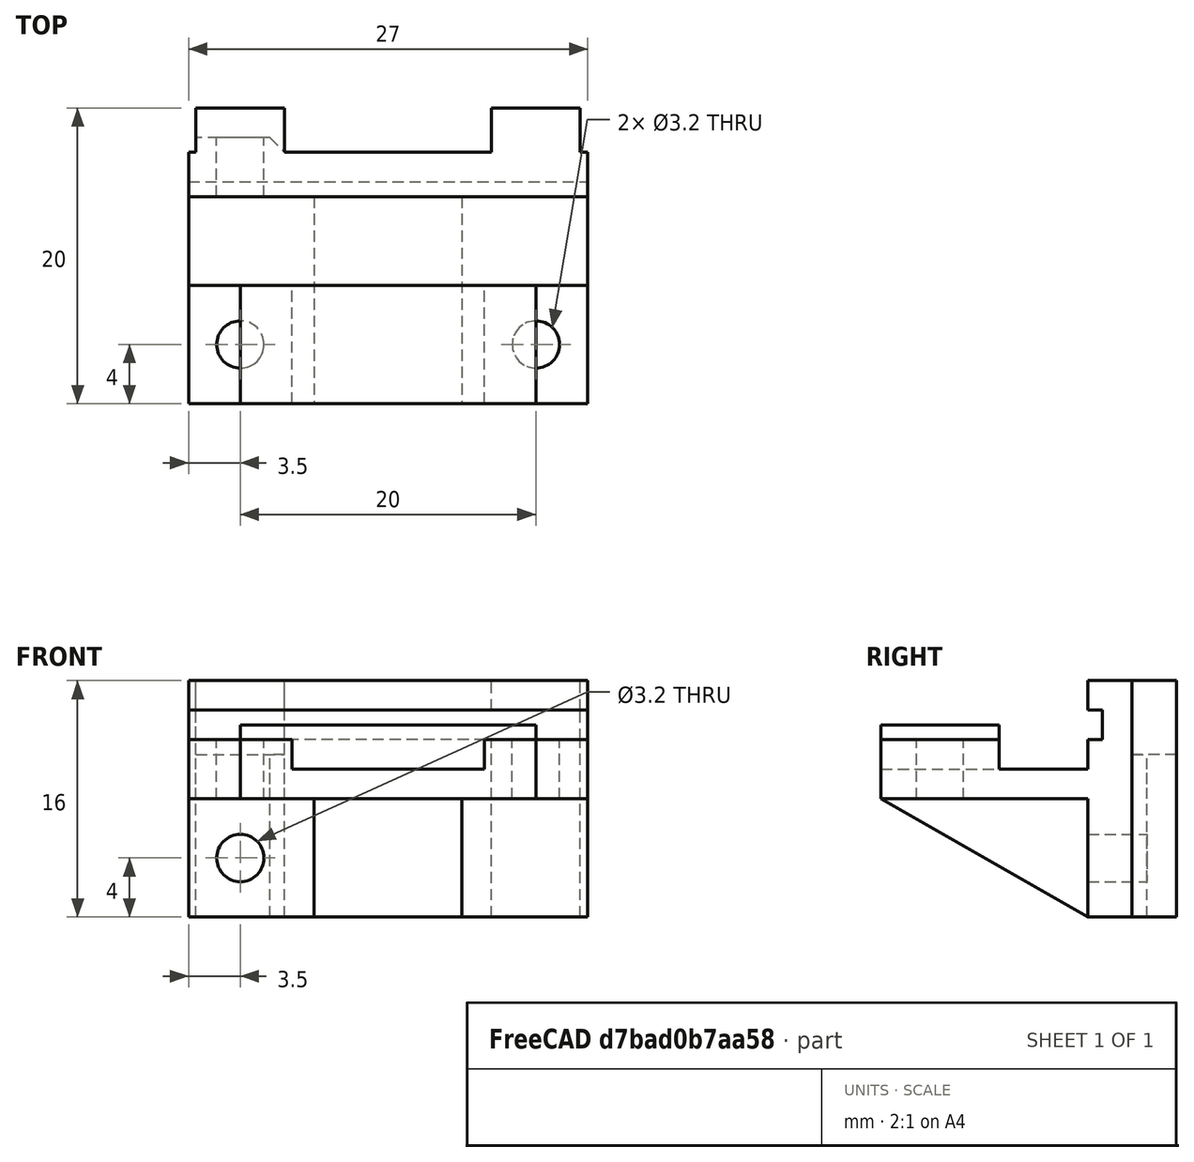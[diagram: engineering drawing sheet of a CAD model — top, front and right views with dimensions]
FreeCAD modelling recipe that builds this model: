
FCSTD DOCUMENT  (FreeCAD 0.18R14555 (Git shallow))
Label: dual-z-motor-mounter
License: All rights reserved
LicenseURL: http://en.wikipedia.org/wiki/All_rights_reserved
objects: Part::Box×15, Part::MultiFuse×5, Part::Cut×5, Part::Cylinder×3, Part::Feature×3, Part::Chamfer×1, Part::MultiCommon×1
note: 33 computed .brp shape members not serialized (recipe doc carries the construction recipe); baked Part::Feature solids carry a one-line shape summary decoded from their .brp

FEATURE [Part::Box] Box  label="Cube"
  AttacherType = Attacher::AttachEngine3D
  Height = 5
  Length = 27
  Width = 15
FEATURE [Part::Box] Box001  label="Cube001"
  AttacherType = Attacher::AttachEngine3D
  Height = 5
  Length = 27
  Placement = pos=(0,15,0) rot=(0,0,1;0rad)
  Width = 2
FEATURE [Part::Box] Box002  label="Cube002"
  AttacherType = Attacher::AttachEngine3D
  Height = 2
  Length = 27
  Placement = pos=(0,15,5) rot=(0,0,1;0rad)
  Width = 2
FEATURE [Part::Box] Box003  label="Cube003"
  AttacherType = Attacher::AttachEngine3D
  Height = 2
  Length = 27
  Placement = pos=(0,14,7) rot=(0,0,1;0rad)
  Width = 3
FEATURE [Part::Box] Box004  label="Cube004"
  AttacherType = Attacher::AttachEngine3D
  Height = 3
  Length = 13
  Placement = pos=(7,0,2) rot=(0,0,1;0rad)
  Width = 8
FEATURE [Part::Box] Box005  label="Cube005"
  AttacherType = Attacher::AttachEngine3D
  Height = 3
  Length = 27
  Placement = pos=(0,8,2) rot=(0,0,1;0rad)
  Width = 6
FEATURE [Part::MultiFuse] Fusion
  Placement = pos=(0,0,1) rot=(0,0,1;0rad)
  Shapes = -> [Box005,Box004]
FEATURE [Part::Box] Box006  label="Cube006"
  AttacherType = Attacher::AttachEngine3D
  Height = 5
  Length = 20
  Placement = pos=(3.5,0,0) rot=(0,0,1;0rad)
  Width = 8
FEATURE [Part::Cylinder] Cylinder
  Angle = 360
  AttacherType = Attacher::AttachEngine3D
  Height = 5
  Placement = pos=(3.5,4,0) rot=(0,0,1;0rad)
  Radius = 1.6
FEATURE [Part::Cylinder] Cylinder001
  Angle = 360
  AttacherType = Attacher::AttachEngine3D
  Height = 5
  Placement = pos=(23.5,4,0) rot=(0,0,1;0rad)
  Radius = 1.6
FEATURE [Part::MultiFuse] Fusion002
  Shapes = -> [Cylinder001,Cylinder]
FEATURE [Part::MultiFuse] Fusion003
  Shapes = -> [Box002,Box,Box001,Box003]
FEATURE [Part::Cut] Cut
  Base = -> Fusion003
  Tool = -> Fusion
FEATURE [Part::Cut] Cut001
  Base = -> Cut
  Tool = -> Fusion002
FEATURE [Part::Box] Box007  label="Cube007"
  AttacherType = Attacher::AttachEngine3D
  Height = 1
  Length = 27
  Width = 17
FEATURE [Part::Cut] Cut002
  Base = -> Cut001
  Placement = pos=(0,0,-1) rot=(0,0,1;0rad)
  Tool = -> Box007
FEATURE [Part::Box] Box008  label="Cube008"
  AttacherType = Attacher::AttachEngine3D
  Height = 8
  Length = 27
  Placement = pos=(0,14,-8) rot=(0,0,1;0rad)
  Width = 3
FEATURE [Part::Box] Box010  label="Cube010"
  AttacherType = Attacher::AttachEngine3D
  Height = 8
  Length = 6
  Placement = pos=(0.5,15,-8) rot=(0,0,1;0rad)
  Width = 3
FEATURE [Part::Box] Box011  label="Cube011"
  AttacherType = Attacher::AttachEngine3D
  Height = 8
  Length = 6
  Placement = pos=(20.5,17,-8) rot=(0,0,1;0rad)
  Width = 3
FEATURE [Part::Box] Box012  label="Cube012"
  AttacherType = Attacher::AttachEngine3D
  Height = 8
  Length = 6
  Placement = pos=(20.5,17,0) rot=(0,0,1;0rad)
  Width = 3
FEATURE [Part::Box] Box013  label="Cube013"
  AttacherType = Attacher::AttachEngine3D
  Height = 8
  Length = 6
  Placement = pos=(0.5,17,0) rot=(0,0,1;0rad)
  Width = 3
FEATURE [Part::Cylinder] Cylinder002
  Angle = 360
  AttacherType = Attacher::AttachEngine3D
  Height = 10
  Placement = pos=(3.5,13,-4) rot=(-1,0,0;1.5708rad)
  Radius = 1.6
FEATURE [Part::Feature] Body001
  Placement = pos=(8.5,-1,10) rot=(0,0,1;0rad)
  shape: bbox 10 x 14 x 8 mm, 5 faces (baked)
FEATURE [Part::Chamfer] Chamfer
  Base = -> Box010
  Edges = 1 edges r=1: [Edge7]
FEATURE [Part::MultiFuse] Fusion004
  Shapes = -> [Chamfer,Box011,Cut002,Box012,Box008,Box013,Body001]
FEATURE [Part::Cut] Cut003
  Base = -> Fusion004
  Tool = -> Cylinder002
FEATURE [Part::Box] Box014  label="Cube014"
  AttacherType = Attacher::AttachEngine3D
  Height = 3
  Length = 10
  Placement = pos=(0,17,0) rot=(0,0,1;0rad)
  Width = 3
FEATURE [Part::Box] Box015  label="Cube015"
  AttacherType = Attacher::AttachEngine3D
  Height = 2
  Length = 10
  Placement = pos=(0,17,-2) rot=(0,0,1;0rad)
  Width = 2
FEATURE [Part::Feature] Cut003001  label="Cut004"
  shape: bbox 27 x 20 x 16 mm, 66 faces (baked)
FEATURE [Part::Cut] Cut003002
  Base = -> Cut003
  Tool = -> Box014
FEATURE [Part::MultiCommon] Common
  Placement = pos=(0,0,2) rot=(0,0,1;0rad)
  Shapes = -> [Box015,Cut003001]
FEATURE [Part::Feature] Common001
  Placement = pos=(0,0,3) rot=(0,0,1;0rad)
  shape: bbox 6 x 1 x 2 mm, 6 faces (baked)
FEATURE [Part::MultiFuse] Fusion005
  Shapes = -> [Common001,Common,Cut003002]
